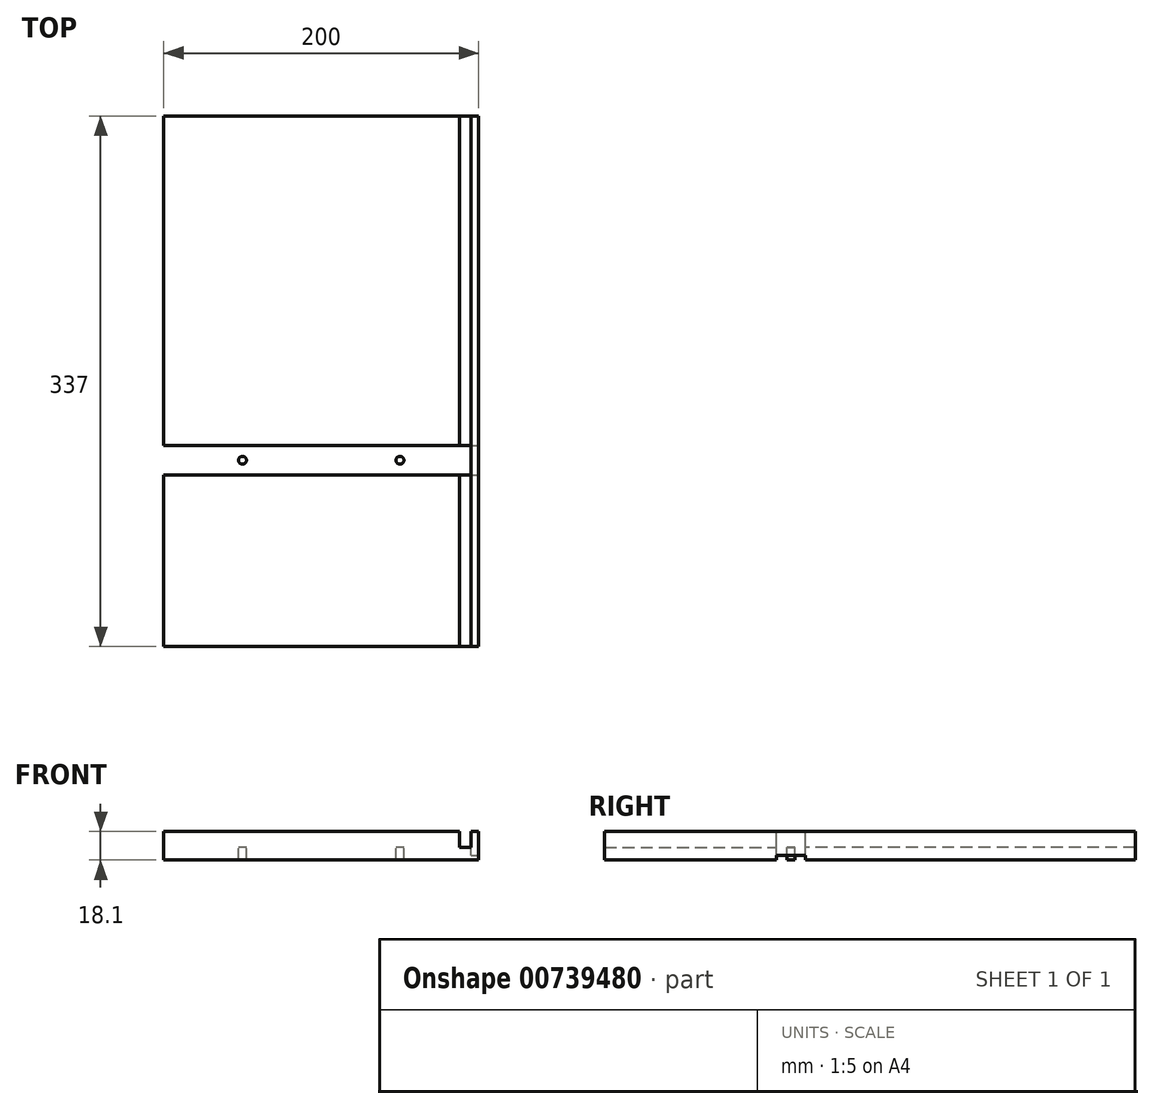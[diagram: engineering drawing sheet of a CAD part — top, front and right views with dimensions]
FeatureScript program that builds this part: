
annotation { "Feature Type Name" : "Feature", "Feature Type Description" : "" }
export const myFeature = defineFeature(function(context is Context, id is Id, definition is map)
    precondition{}
    {
        {
            var Q0;
            Q0=qCreatedBy(makeId("Top.planeOp"),FACE);
            var sketch = newSketch(context, id + "F0", { "sketchPlane" : qUnion([Q0])});
            skLineSegment(sketch, "E0.bottom", {"start": v(100, 168.5) * mm, "end": v(-100, 168.5) * mm});
            skLineSegment(sketch, "E0.top", {"start": v(100, -168.5) * mm, "end": v(-100, -168.5) * mm});
            skLineSegment(sketch, "E0.left", {"start": v(100, 168.5) * mm, "end": v(100, -168.5) * mm});
            skLineSegment(sketch, "E0.right", {"start": v(-100, 168.5) * mm, "end": v(-100, -168.5) * mm});
            skPoint(sketch, "E0.middle", {"position": v(0, 0) * mm});
            skSolve(sketch);
        }
        {
            var Q0;
            Q0=makeQuery(id+"F0.imprint","IMPRINT",FACE,{"disambiguationData":[TD([[makeQuery(id+"F0.imprint","IMPRINT",EDGE,{"derivedFrom":sQuery(id+"F0.wireOp",EDGE,"E0.bottom")}),1.0]])]});
            extrude(context, id + "F1", {"entities" : qUnion([Q0]), "depth" : 18.1 * mm, "offsetDistance" : 25 * mm});
        }
        {
            var Q0;
            Q0=makeQuery(id+"F1.opExtrude","CAP_FACE",FACE,{"disambiguationData":[OSD([sQuery(id+"F0.wireOp",EDGE,"E0.bottom"),sQuery(id+"F0.wireOp",EDGE,"E0.top"),sQuery(id+"F0.wireOp",EDGE,"E0.left"),sQuery(id+"F0.wireOp",EDGE,"E0.right")])],"isStart":false});
            var sketch = newSketch(context, id + "F2", { "sketchPlane" : qUnion([Q0])});
            skLineSegment(sketch, "E1", {"start": v(-100, -168.5) * mm, "end": v(-100, -59.5) * mm});
            skLineSegment(sketch, "E2", {"start": v(-100, -59.5) * mm, "end": v(100, -59.5) * mm});
            skLineSegment(sketch, "E3", {"start": v(100, -59.5) * mm, "end": v(100, -40.9) * mm});
            skLineSegment(sketch, "E4", {"start": v(100, -40.9) * mm, "end": v(-100, -40.9) * mm});
            skLineSegment(sketch, "E5", {"start": v(-100, -40.9) * mm, "end": v(-100, -59.5) * mm});
            skLineSegment(sketch, "E6.1.0.0", {"start": v(-75, -168.5) * mm, "end": v(-75, -59.5) * mm});
            skLineSegment(sketch, "E6.1.0.1", {"start": v(-75, -59.5) * mm, "end": v(125, -59.5) * mm});
            skLineSegment(sketch, "E6.1.0.2", {"start": v(125, -59.5) * mm, "end": v(125, -40.9) * mm});
            skLineSegment(sketch, "E6.1.0.3", {"start": v(125, -40.9) * mm, "end": v(-75, -40.9) * mm});
            skLineSegment(sketch, "E6.1.0.4", {"start": v(-75, -40.9) * mm, "end": v(-75, -59.5) * mm});
            skLineSegment(sketch, "E6.2.0.0", {"start": v(-50, -168.5) * mm, "end": v(-50, -59.5) * mm});
            skLineSegment(sketch, "E6.2.0.1", {"start": v(-50, -59.5) * mm, "end": v(150, -59.5) * mm});
            skLineSegment(sketch, "E6.2.0.2", {"start": v(150, -59.5) * mm, "end": v(150, -40.9) * mm});
            skLineSegment(sketch, "E6.2.0.3", {"start": v(150, -40.9) * mm, "end": v(-50, -40.9) * mm});
            skLineSegment(sketch, "E6.2.0.4", {"start": v(-50, -40.9) * mm, "end": v(-50, -59.5) * mm});
            skLineSegment(sketch, "E6.direction1", {"start": v(-100, -168.5) * mm, "end": v(-75, -168.5) * mm, "construction": true});
            skLineSegment(sketch, "E7", {"start": v(-100, 168.5) * mm, "end": v(-100, 158.5) * mm});
            skLineSegment(sketch, "E8", {"start": v(-100, 158.5) * mm, "end": v(-100, 139.9) * mm});
            skPoint(sketch, "E9.end.orphan", {"position": v(100, 158.5) * mm});
            skSolve(sketch);
        }
        {
            var Q0;
            Q0=qSketchRegion(id+"F2",true);
            extrude(context, id + "F3", {"entities" : qUnion([Q0]), "operationType" : NewBodyOperationType.REMOVE, "oppositeDirection" : true, "depth" : 10 * mm, "offsetDistance" : 25 * mm});
        }
        {
            var Q0;
            Q0=makeQuery(id+"F3.boolean.opBoolean","COPY",FACE,{"derivedFrom":makeQuery(id+"F3.opExtrude","CAP_FACE",FACE,{"disambiguationData":[OSD([sQuery(id+"F2.wireOp",EDGE,"E2"),sQuery(id+"F2.wireOp",EDGE,"E4"),sQuery(id+"F2.wireOp",EDGE,"E5"),sQuery(id+"F2.wireOp",EDGE,"E6.1.0.1"),sQuery(id+"F2.wireOp",EDGE,"E6.1.0.3"),sQuery(id+"F2.wireOp",EDGE,"E6.2.0.1"),sQuery(id+"F2.wireOp",EDGE,"E6.2.0.2"),sQuery(id+"F2.wireOp",EDGE,"E6.2.0.3")])],"isStart":false})});
            var sketch = newSketch(context, id + "F4", { "sketchPlane" : qUnion([Q0])});
            skLineSegment(sketch, "E10", {"start": v(-100, -50.2) * mm, "end": v(100, -50.2) * mm});
            skLineSegment(sketch, "E11", {"start": v(100, -50.2) * mm, "end": v(50, -50.2) * mm});
            skLineSegment(sketch, "E12", {"start": v(-100, -50.2) * mm, "end": v(-50, -50.2) * mm});
            skCircle(sketch, "E13", {"center": v(-50, -50.2) * mm, "radius": 2.5 * mm});
            skCircle(sketch, "E14", {"center": v(50, -50.2) * mm, "radius": 2.5 * mm});
            skSolve(sketch);
        }
        {
            var Q0;
            {var subQ0=sQuery(id+"F4.wireOp",EDGE,"E12");var subQ1=sQuery(id+"F4.wireOp",EDGE,"E10");var subQ2=makeQuery(id+"F4.imprint","INTERSECT",VERTEX,{"derivedFrom":[subQ1,subQ0]});Q0=makeQuery(id+"F4.imprint","IMPRINT",FACE,{"disambiguationData":[TD([[makeQuery(id+"F4.imprint","IMPRINT",EDGE,{"disambiguationData":[TD([[subQ2,-1.0]])],"derivedFrom":subQ1}),1.0]])]});}
            var Q1;
            {var subQ0=sQuery(id+"F4.wireOp",EDGE,"E12");var subQ1=sQuery(id+"F4.wireOp",EDGE,"E10");var subQ2=makeQuery(id+"F4.imprint","INTERSECT",VERTEX,{"derivedFrom":[subQ1,subQ0]});Q1=makeQuery(id+"F4.imprint","IMPRINT",FACE,{"disambiguationData":[TD([[makeQuery(id+"F4.imprint","IMPRINT",EDGE,{"disambiguationData":[TD([[subQ2,-1.0]])],"derivedFrom":subQ1}),-1.0]])]});}
            var Q2;
            {var subQ0=sQuery(id+"F4.wireOp",EDGE,"E11");var subQ1=sQuery(id+"F4.wireOp",EDGE,"E10");var subQ2=makeQuery(id+"F4.imprint","INTERSECT",VERTEX,{"derivedFrom":[subQ1,subQ0]});Q2=makeQuery(id+"F4.imprint","IMPRINT",FACE,{"disambiguationData":[TD([[makeQuery(id+"F4.imprint","IMPRINT",EDGE,{"disambiguationData":[TD([[subQ2,1.0]])],"derivedFrom":subQ1}),1.0]])]});}
            var Q3;
            {var subQ0=sQuery(id+"F4.wireOp",EDGE,"E11");var subQ1=sQuery(id+"F4.wireOp",EDGE,"E10");var subQ2=makeQuery(id+"F4.imprint","INTERSECT",VERTEX,{"derivedFrom":[subQ1,subQ0]});Q3=makeQuery(id+"F4.imprint","IMPRINT",FACE,{"disambiguationData":[TD([[makeQuery(id+"F4.imprint","IMPRINT",EDGE,{"disambiguationData":[TD([[subQ2,1.0]])],"derivedFrom":subQ1}),-1.0]])]});}
            extrude(context, id + "F5", {"entities" : qUnion([Q0, Q1, Q2, Q3]), "operationType" : NewBodyOperationType.REMOVE, "oppositeDirection" : true, "depth" : 25 * mm, "offsetDistance" : 25 * mm});
        }
        {
            var Q0;
            {var subQ0=sQuery(id+"F0.wireOp",EDGE,"E0.bottom");var subQ1=sQuery(id+"F0.wireOp",EDGE,"E0.right");var subQ2=sQuery(id+"F0.wireOp",EDGE,"E0.left");Q0=makeQuery(id+"F3.boolean.opBoolean","SPLIT",FACE,{"disambiguationData":[TD([makeQuery(id+"F1.opExtrude","SWEPT_FACE",FACE,{"disambiguationData":[OSD([subQ0])]})])],"derivedFrom":makeQuery(id+"F1.opExtrude","CAP_FACE",FACE,{"disambiguationData":[OSD([subQ0,sQuery(id+"F0.wireOp",EDGE,"E0.top"),subQ2,subQ1])],"isStart":false})});}
            var sketch = newSketch(context, id + "F6", { "sketchPlane" : qUnion([Q0])});
            skLineSegment(sketch, "E15", {"start": v(100, 168.5) * mm, "end": v(95, 168.5) * mm});
            skLineSegment(sketch, "E16", {"start": v(95, 168.5) * mm, "end": v(88, 168.5) * mm});
            skLineSegment(sketch, "E17", {"start": v(95, 168.5) * mm, "end": v(95, -40.9) * mm});
            skLineSegment(sketch, "E18", {"start": v(88, 168.5) * mm, "end": v(88, -40.9) * mm});
            skSolve(sketch);
        }
        {
            var Q0;
            {var subQ0=sQuery(id+"F0.wireOp",EDGE,"E0.top");var subQ1=sQuery(id+"F0.wireOp",EDGE,"E0.left");var subQ2=sQuery(id+"F0.wireOp",EDGE,"E0.right");Q0=makeQuery(id+"F3.boolean.opBoolean","SPLIT",FACE,{"disambiguationData":[TD([makeQuery(id+"F1.opExtrude","SWEPT_FACE",FACE,{"disambiguationData":[OSD([subQ0])]})])],"derivedFrom":makeQuery(id+"F1.opExtrude","CAP_FACE",FACE,{"disambiguationData":[OSD([sQuery(id+"F0.wireOp",EDGE,"E0.bottom"),subQ0,subQ1,subQ2])],"isStart":false})});}
            var sketch = newSketch(context, id + "F7", { "sketchPlane" : qUnion([Q0])});
            skLineSegment(sketch, "E19", {"start": v(100, -168.5) * mm, "end": v(95, -168.5) * mm});
            skLineSegment(sketch, "E20", {"start": v(95, -168.5) * mm, "end": v(88, -168.5) * mm});
            skLineSegment(sketch, "E21", {"start": v(88, -168.5) * mm, "end": v(88, -59.5) * mm});
            skLineSegment(sketch, "E22", {"start": v(95, -168.5) * mm, "end": v(95, -59.5) * mm});
            skSolve(sketch);
        }
        {
            var Q0;
            Q0=makeQuery(id+"F7.imprint","IMPRINT",FACE,{"disambiguationData":[TD([[makeQuery(id+"F7.imprint","IMPRINT",EDGE,{"derivedFrom":sQuery(id+"F7.wireOp",EDGE,"E20")}),-1.0]])]});
            var Q1;
            Q1=makeQuery(id+"F6.imprint","IMPRINT",FACE,{"disambiguationData":[TD([[makeQuery(id+"F6.imprint","IMPRINT",EDGE,{"derivedFrom":sQuery(id+"F6.wireOp",EDGE,"E16")}),1.0]])]});
            extrude(context, id + "F8", {"entities" : qUnion([Q0, Q1]), "operationType" : NewBodyOperationType.REMOVE, "oppositeDirection" : true, "depth" : 10 * mm, "offsetDistance" : 25 * mm});
        }
        {
            var Q0;
            {var subQ0=sQuery(id+"F0.wireOp",EDGE,"E0.top");var subQ1=makeQuery(id+"F1.opExtrude","SWEPT_FACE",FACE,{"disambiguationData":[OSD([subQ0])]});var subQ2=sQuery(id+"F0.wireOp",EDGE,"E0.left");var subQ3=makeQuery(id+"F1.opExtrude","SWEPT_FACE",FACE,{"disambiguationData":[OSD([subQ2])]});var subQ5=sQuery(id+"F0.wireOp",EDGE,"E0.right");Q0=makeQuery(id+"F8.boolean.opBoolean","SPLIT",FACE,{"disambiguationData":[TD([subQ3])],"derivedFrom":makeQuery(id+"F3.boolean.opBoolean","SPLIT",FACE,{"disambiguationData":[TD([subQ1])],"derivedFrom":makeQuery(id+"F1.opExtrude","CAP_FACE",FACE,{"disambiguationData":[OSD([sQuery(id+"F0.wireOp",EDGE,"E0.bottom"),subQ0,subQ2,subQ5])],"isStart":false})})});}
            var sketch = newSketch(context, id + "F9", { "sketchPlane" : qUnion([Q0])});
            skLineSegment(sketch, "E23.bottom", {"start": v(95, -59.5) * mm, "end": v(100, -59.5) * mm});
            skLineSegment(sketch, "E23.top", {"start": v(95, -40.9) * mm, "end": v(100, -40.9) * mm});
            skLineSegment(sketch, "E23.left", {"start": v(95, -59.5) * mm, "end": v(95, -40.9) * mm});
            skLineSegment(sketch, "E23.right", {"start": v(100, -59.5) * mm, "end": v(100, -40.9) * mm});
            skSolve(sketch);
        }
        {
            var Q0;
            Q0 = qSketchRegion(id + "F9", true);
            extrude(context, id + "F10", {"entities" : qUnion([Q0]), "operationType" : NewBodyOperationType.ADD, "oppositeDirection" : true, "depth" : 15.1 * mm, "offsetDistance" : 25 * mm});
        }
    });
